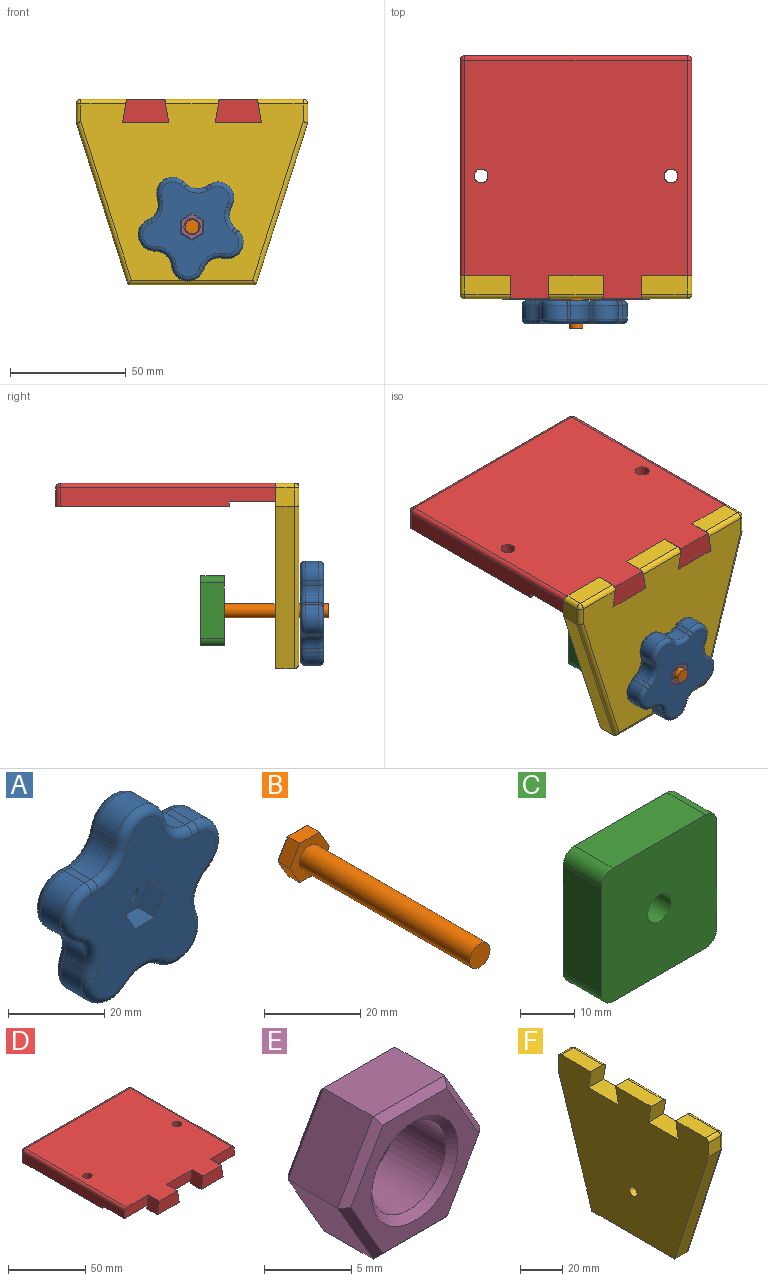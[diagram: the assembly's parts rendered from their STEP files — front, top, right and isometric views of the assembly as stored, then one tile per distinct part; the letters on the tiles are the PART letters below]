
ASSEMBLY  parts=6 mates=9
PART A: 70 faces, bbox 46.8x10x45.2 mm
  f0: plane 41.61x40.06mm, normal (0,-1,0), area 933.1mm2, adj f22,f23,f24,f25,f26,f27,f30,f31
  f1: plane 6x1.9mm, normal (0,0,1), area 11.4mm2, adj f12,f14,f34,f54
  f2: plane 6x1.81mm, normal (0.95,0,0.31), area 11.4mm2, adj f12,f15,f30,f50
  f3: plane 6x1.81mm, normal (-0.95,0,0.31), area 11.4mm2, adj f15,f16,f33,f53
  f4: plane 6x1.9mm, normal (0,0,1), area 11.4mm2, adj f16,f17,f37,f57
  f5: plane 6x1.54mm, normal (-0.59,0,-0.81), area 11.4mm2, adj f17,f18,f41,f61
  f6: plane 6x1.81mm, normal (-0.95,0,0.31), area 11.4mm2, adj f18,f20,f45,f65
  f7: plane 6x1.54mm, normal (0.59,0,-0.81), area 11.4mm2, adj f19,f20,f49,f69
  f8: plane 6x1.54mm, normal (-0.59,0,-0.81), area 11.4mm2, adj f19,f21,f46,f66
  f9: plane 6x1.81mm, normal (0.95,0,0.31), area 11.4mm2, adj f13,f21,f42,f62
  f10: plane 6x1.54mm, normal (0.59,0,-0.81), area 11.4mm2, adj f13,f14,f38,f58
  f11: plane 41.61x40.06mm, normal (0,1,0), area 991.5mm2, adj f29,f50,f51,f52,f53,f54,f55,f56
  f12: cylinder r=7mm len=6.66mm, axis (0,-1,0), area 52.8mm2, adj f1,f2,f32,f52
  f13: cylinder r=7mm len=7.83mm, axis (0,1,0), area 52.8mm2, adj f9,f10,f40,f60
  f14: cylinder r=7mm len=12.66mm, axis (0,-1,0), area 105.6mm2, adj f1,f10,f36,f56
  f15: cylinder r=7mm len=13.31mm, axis (0,-1,0), area 105.6mm2, adj f2,f3,f31,f51
  f16: cylinder r=7mm len=6.66mm, axis (0,1,0), area 52.8mm2, adj f3,f4,f35,f55
  f17: cylinder r=7mm len=12.66mm, axis (0,1,0), area 105.6mm2, adj f4,f5,f39,f59
  f18: cylinder r=7mm len=7.83mm, axis (0,1,0), area 52.8mm2, adj f5,f6,f43,f63
  f19: cylinder r=7mm len=8.23mm, axis (0,1,0), area 52.8mm2, adj f7,f8,f48,f68
  f20: cylinder r=7mm len=11.11mm, axis (0,1,0), area 105.6mm2, adj f6,f7,f47,f67
  f21: cylinder r=7mm len=11.11mm, axis (0,1,0), area 105.6mm2, adj f8,f9,f44,f64
  f22: plane 5x5mm, normal (0.87,0,-0.5), area 28.9mm2, adj f0,f23,f27,f28
  f23: plane 5x5mm, normal (0.87,0,0.5), area 28.9mm2, adj f0,f22,f24,f28
  f24: plane 5.77x5mm, normal (0,0,1), area 28.9mm2, adj f0,f23,f25,f28
  f25: plane 5x5mm, normal (-0.87,0,0.5), area 28.9mm2, adj f0,f24,f26,f28
  f26: plane 5x5mm, normal (-0.87,0,-0.5), area 28.9mm2, adj f0,f25,f27,f28
  f27: plane 5.77x5mm, normal (0,0,-1), area 28.9mm2, adj f0,f22,f26,f28
  f28: plane 11.55x10mm, normal (0,-1,0), area 58.3mm2, adj f22,f23,f24,f25,f26,f27,f29
  f29: cylinder r=3mm len=6mm, axis (0,-1,0), area 94.2mm2, adj f11,f28
  f30: cylinder r=2mm len=2.49mm, axis (0.31,0,-0.95), area 6mm2, adj f0,f2,f31,f32
  f31: torus R=5mm, axis (0,-1,0), area 49.5mm2, adj f0,f15,f30,f33
  f32: torus R=9mm, axis (0,-1,0), area 30.5mm2, adj f0,f12,f30,f34
  f33: cylinder r=2mm len=2.49mm, axis (0.31,0,0.95), area 6mm2, adj f0,f3,f31,f35
  f34: cylinder r=2mm len=2mm, axis (1,0,0), area 6mm2, adj f0,f1,f32,f36
  f35: torus R=9mm, axis (0,-1,0), area 30.5mm2, adj f0,f16,f33,f37
  f36: torus R=5mm, axis (0,-1,0), area 49.5mm2, adj f0,f14,f34,f38
  f37: cylinder r=2mm len=2mm, axis (1,0,0), area 6mm2, adj f0,f4,f35,f39
  f38: cylinder r=2mm len=2.74mm, axis (-0.81,0,-0.59), area 6mm2, adj f0,f10,f36,f40
  f39: torus R=5mm, axis (0,-1,0), area 49.5mm2, adj f0,f17,f37,f41
  f40: torus R=9mm, axis (0,-1,0), area 30.5mm2, adj f0,f13,f38,f42
  f41: cylinder r=2mm len=2.74mm, axis (-0.81,0,0.59), area 6mm2, adj f0,f5,f39,f43
  f42: cylinder r=2mm len=2.49mm, axis (0.31,0,-0.95), area 6mm2, adj f0,f9,f40,f44
  f43: torus R=9mm, axis (0,-1,0), area 30.5mm2, adj f0,f18,f41,f45
  f44: torus R=5mm, axis (0,-1,0), area 49.5mm2, adj f0,f21,f42,f46
  f45: cylinder r=2mm len=2.49mm, axis (0.31,0,0.95), area 6mm2, adj f0,f6,f43,f47
  f46: cylinder r=2mm len=2.74mm, axis (-0.81,0,0.59), area 6mm2, adj f0,f8,f44,f48
  f47: torus R=5mm, axis (0,-1,0), area 49.5mm2, adj f0,f20,f45,f49
  f48: torus R=9mm, axis (0,-1,0), area 30.5mm2, adj f0,f19,f46,f49
  f49: cylinder r=2mm len=2.74mm, axis (-0.81,0,-0.59), area 6mm2, adj f0,f7,f47,f48
  f50: cylinder r=2mm len=2.49mm, axis (-0.31,0,0.95), area 6mm2, adj f2,f11,f51,f52
  f51: torus R=5mm, axis (0,-1,0), area 49.5mm2, adj f11,f15,f50,f53
  f52: torus R=9mm, axis (0,-1,0), area 30.5mm2, adj f11,f12,f50,f54
  f53: cylinder r=2mm len=2.49mm, axis (-0.31,0,-0.95), area 6mm2, adj f3,f11,f51,f55
  f54: cylinder r=2mm len=2mm, axis (-1,0,0), area 6mm2, adj f1,f11,f52,f56
  f55: torus R=9mm, axis (0,-1,0), area 30.5mm2, adj f11,f16,f53,f57
  f56: torus R=5mm, axis (0,-1,0), area 49.5mm2, adj f11,f14,f54,f58
  f57: cylinder r=2mm len=2mm, axis (-1,0,0), area 6mm2, adj f4,f11,f55,f59
  f58: cylinder r=2mm len=2.74mm, axis (0.81,0,0.59), area 6mm2, adj f10,f11,f56,f60
  f59: torus R=5mm, axis (0,-1,0), area 49.5mm2, adj f11,f17,f57,f61
  f60: torus R=9mm, axis (0,-1,0), area 30.5mm2, adj f11,f13,f58,f62
  f61: cylinder r=2mm len=2.74mm, axis (0.81,0,-0.59), area 6mm2, adj f5,f11,f59,f63
  f62: cylinder r=2mm len=2.49mm, axis (-0.31,0,0.95), area 6mm2, adj f9,f11,f60,f64
  f63: torus R=9mm, axis (0,-1,0), area 30.5mm2, adj f11,f18,f61,f65
  f64: torus R=5mm, axis (0,-1,0), area 49.5mm2, adj f11,f21,f62,f66
  f65: cylinder r=2mm len=2.49mm, axis (-0.31,0,-0.95), area 6mm2, adj f6,f11,f63,f67
  f66: cylinder r=2mm len=2.74mm, axis (0.81,0,-0.59), area 6mm2, adj f8,f11,f64,f68
  f67: torus R=5mm, axis (0,-1,0), area 49.5mm2, adj f11,f20,f65,f69
  f68: torus R=9mm, axis (0,-1,0), area 30.5mm2, adj f11,f19,f66,f69
  f69: cylinder r=2mm len=2.74mm, axis (0.81,0,0.59), area 6mm2, adj f7,f11,f67,f68
PART B: 16 faces, bbox 11.5x54x10 mm
  f0: plane 5x3.5mm, normal (-0.87,0,0.5), area 20.2mm2, adj f1,f5,f7,f15
  f1: plane 5x3.5mm, normal (-0.87,0,-0.5), area 20.2mm2, adj f0,f2,f7,f13
  f2: plane 5.77x3.5mm, normal (0,0,-1), area 20.2mm2, adj f1,f3,f7,f11
  f3: plane 5x3.5mm, normal (0.87,0,-0.5), area 20.2mm2, adj f2,f4,f7,f10
  f4: plane 5x3.5mm, normal (0.87,0,0.5), area 20.2mm2, adj f3,f5,f7,f12
  f5: plane 5.77x3.5mm, normal (0,0,1), area 20.2mm2, adj f0,f4,f7,f14
  f6: plane 10.39x9mm, normal (0,1,0), area 70.1mm2, adj f10,f11,f12,f13,f14,f15
  f7: plane 11.55x10mm, normal (0,-1,0), area 58.3mm2, adj f0,f1,f2,f3,f4,f5,f8
  f8: cylinder r=3mm len=50mm, axis (0,1,0), area 942.5mm2, adj f7,f9
  f9: plane 6x6mm, normal (0,-1,0), area 28.3mm2, adj f8
  f10: plane 5x3.18mm, normal (0.61,0.71,-0.35), area 3.9mm2, adj f3,f6,f11,f12
  f11: plane 5.77x0.5mm, normal (0,0.71,-0.71), area 3.9mm2, adj f2,f6,f10,f13
  f12: plane 5x3.18mm, normal (0.61,0.71,0.35), area 3.9mm2, adj f4,f6,f10,f14
  f13: plane 5x3.18mm, normal (-0.61,0.71,-0.35), area 3.9mm2, adj f1,f6,f11,f15
  f14: plane 5.77x0.5mm, normal (0,0.71,0.71), area 3.9mm2, adj f5,f6,f12,f15
  f15: plane 5x3.18mm, normal (-0.61,0.71,0.35), area 3.9mm2, adj f0,f6,f13,f14
PART C: 18 faces, bbox 30x10x30 mm
  f0: plane 30x30mm, normal (0,1,0), area 805.7mm2, adj f1,f2,f3,f4,f6,f7,f8,f9
  f1: plane 24x10mm, normal (0,0,-1), area 240mm2, adj f0,f5,f14,f17
  f2: plane 24x10mm, normal (1,0,0), area 240mm2, adj f0,f5,f14,f15
  f3: plane 24x10mm, normal (0,0,1), area 240mm2, adj f0,f5,f15,f16
  f4: plane 24x10mm, normal (-1,0,0), area 240mm2, adj f0,f5,f16,f17
  f5: plane 30x30mm, normal (0,-1,0), area 864mm2, adj f1,f2,f3,f4,f13,f14,f15,f16
  f6: plane 5x5mm, normal (-0.87,0,-0.5), area 28.9mm2, adj f0,f7,f11,f12
  f7: plane 5x5mm, normal (-0.87,0,0.5), area 28.9mm2, adj f0,f6,f8,f12
  f8: plane 5.77x5mm, normal (0,0,1), area 28.9mm2, adj f0,f7,f9,f12
  f9: plane 5x5mm, normal (0.87,0,0.5), area 28.9mm2, adj f0,f8,f10,f12
  f10: plane 5x5mm, normal (0.87,0,-0.5), area 28.9mm2, adj f0,f9,f11,f12
  f11: plane 5.77x5mm, normal (0,0,-1), area 28.9mm2, adj f0,f6,f10,f12
  f12: plane 11.55x10mm, normal (0,1,0), area 58.3mm2, adj f6,f7,f8,f9,f10,f11,f13
  f13: cylinder r=3mm len=6mm, axis (0,1,0), area 94.2mm2, adj f5,f12
  f14: cylinder r=3mm len=10mm, axis (0,1,0), area 47.1mm2, adj f0,f1,f2,f5
  f15: cylinder r=3mm len=10mm, axis (0,-1,0), area 47.1mm2, adj f0,f2,f3,f5
  f16: cylinder r=3mm len=10mm, axis (0,1,0), area 47.1mm2, adj f0,f3,f4,f5
  f17: cylinder r=3mm len=10mm, axis (0,-1,0), area 47.1mm2, adj f0,f1,f4,f5
PART D: 29 faces, bbox 100x105x10 mm
  f0: plane 100x75mm, normal (0,0,-1), area 7441.7mm2, adj f9,f10,f11,f12,f13,f18,f24,f27
  f1: plane 20x10mm, normal (0,0,-1), area 200mm2, adj f5,f15,f17,f25
  f2: plane 23.53x8mm, normal (0,-1,0), area 176.9mm2, adj f7,f14,f15,f28
  f3: plane 21.76x8mm, normal (0,-1,0), area 167.6mm2, adj f7,f11,f16,f19,f28
  f4: plane 21.76x8mm, normal (0,-1,0), area 167.6mm2, adj f7,f10,f17,f22,f28
  f5: plane 20x10mm, normal (0,-1,0), area 182.4mm2, adj f1,f7,f15,f17
  f6: plane 20x10mm, normal (0,-1,0), area 182.4mm2, adj f7,f8,f14,f16
  f7: plane 103x96mm, normal (0,0,1), area 9200.9mm2, adj f2,f3,f4,f5,f6,f12,f13,f14
  f8: plane 20x10mm, normal (0,0,-1), area 200mm2, adj f6,f14,f16,f26
  f9: plane 96x8mm, normal (0,1,0), area 768mm2, adj f0,f18,f21,f24
  f10: plane 93x8mm, normal (-1,0,0), area 704mm2, adj f0,f4,f22,f24,f27,f28
  f11: plane 93x8mm, normal (1,0,0), area 704mm2, adj f0,f3,f18,f19,f27,f28
  f12: cylinder r=3mm len=10mm, axis (0,0,1), area 188.5mm2, adj f0,f7
  f13: cylinder r=3mm len=10mm, axis (0,0,1), area 188.5mm2, adj f0,f7
  f14: plane 10x10mm, normal (-0.98,0,0.17), area 101.5mm2, adj f2,f6,f7,f8,f26
  f15: plane 10x10mm, normal (0.98,0,0.17), area 101.5mm2, adj f1,f2,f5,f7,f25
  f16: plane 10x10mm, normal (0.98,0,0.17), area 101.5mm2, adj f3,f6,f7,f8,f26
  f17: plane 10x10mm, normal (-0.98,0,0.17), area 101.5mm2, adj f1,f4,f5,f7,f25
  f18: cylinder r=2mm len=8mm, axis (0,0,1), area 25.1mm2, adj f0,f9,f11,f20
  f19: cylinder r=2mm len=93mm, axis (0,-1,0), area 292.2mm2, adj f3,f7,f11,f20
  f20: sphere r=2mm, area 6.3mm2, adj f18,f19,f21
  f21: cylinder r=2mm len=96mm, axis (1,0,0), area 301.6mm2, adj f7,f9,f20,f23
  f22: cylinder r=2mm len=93mm, axis (0,1,0), area 292.2mm2, adj f4,f7,f10,f23
  f23: sphere r=2mm, area 6.3mm2, adj f21,f22,f24
  f24: cylinder r=2mm len=8mm, axis (0,0,-1), area 25.1mm2, adj f0,f9,f10,f23
  f25: plane 20x2mm, normal (0,1,0), area 39.3mm2, adj f1,f15,f17,f28
  f26: plane 20x2mm, normal (0,1,0), area 39.3mm2, adj f8,f14,f16,f28
  f27: plane 100x2mm, normal (0,-1,0), area 200mm2, adj f0,f10,f11,f28
  f28: plane 100x20mm, normal (0,0,-1), area 2000mm2, adj f2,f3,f4,f10,f11,f25,f26,f27
PART E: 23 faces, bbox 11.5x5x10 mm
  f0: plane 5x4mm, normal (-0.87,0,0.5), area 23.1mm2, adj f1,f6,f15,f22
  f1: plane 5x4mm, normal (-0.87,0,-0.5), area 23.1mm2, adj f0,f2,f13,f20
  f2: plane 5.77x4mm, normal (0,0,-1), area 23.1mm2, adj f1,f3,f11,f18
  f3: plane 5x4mm, normal (0.87,0,-0.5), area 23.1mm2, adj f2,f4,f10,f17
  f4: plane 5x4mm, normal (0.87,0,0.5), area 23.1mm2, adj f3,f6,f12,f19
  f5: cylinder r=3mm len=6mm, axis (0,1,0), area 75.4mm2, adj f9,f16
  f6: plane 5.77x4mm, normal (0,0,1), area 23.1mm2, adj f0,f4,f14,f21
  f7: plane 10.39x9mm, normal (0,-1,0), area 31.7mm2, adj f16,f17,f18,f19,f20,f21,f22
  f8: plane 10.39x9mm, normal (0,1,0), area 31.7mm2, adj f9,f10,f11,f12,f13,f14,f15
  f9: cone r=3.5mm half-angle=45deg, axis (0,1,0), area 14.4mm2, adj f5,f8
  f10: plane 5x3.18mm, normal (0.61,0.71,-0.35), area 3.9mm2, adj f3,f8,f11,f12
  f11: plane 5.77x0.5mm, normal (0,0.71,-0.71), area 3.9mm2, adj f2,f8,f10,f13
  f12: plane 5x3.18mm, normal (0.61,0.71,0.35), area 3.9mm2, adj f4,f8,f10,f14
  f13: plane 5x3.18mm, normal (-0.61,0.71,-0.35), area 3.9mm2, adj f1,f8,f11,f15
  f14: plane 5.77x0.5mm, normal (0,0.71,0.71), area 3.9mm2, adj f6,f8,f12,f15
  f15: plane 5x3.18mm, normal (-0.61,0.71,0.35), area 3.9mm2, adj f0,f8,f13,f14
  f16: cone r=3mm half-angle=45deg, axis (0,-1,0), area 14.4mm2, adj f5,f7
  f17: plane 5x3.18mm, normal (0.61,-0.71,-0.35), area 3.9mm2, adj f3,f7,f18,f19
  f18: plane 5.77x0.5mm, normal (0,-0.71,-0.71), area 3.9mm2, adj f2,f7,f17,f20
  f19: plane 5x3.18mm, normal (0.61,-0.71,0.35), area 3.9mm2, adj f4,f7,f17,f21
  f20: plane 5x3.18mm, normal (-0.61,-0.71,-0.35), area 3.9mm2, adj f1,f7,f18,f22
  f21: plane 5.77x0.5mm, normal (0,-0.71,0.71), area 3.9mm2, adj f6,f7,f19,f22
  f22: plane 5x3.18mm, normal (-0.61,-0.71,0.35), area 3.9mm2, adj f0,f7,f20,f21
PART F: 29 faces, bbox 10x100x80 mm
  f0: plane 8x8mm, normal (0,1,0), area 64mm2, adj f13,f15,f24,f27
  f1: plane 19.76x8mm, normal (0,0,1), area 158.1mm2, adj f2,f15,f25,f27
  f2: plane 10x10mm, normal (0,-0.98,-0.17), area 100.7mm2, adj f1,f3,f14,f15,f25
  f3: plane 20x10mm, normal (0,0,1), area 200mm2, adj f2,f4,f14,f15
  f4: plane 10x10mm, normal (0,0.98,-0.17), area 100.7mm2, adj f3,f5,f14,f15,f28
  f5: plane 23.53x8mm, normal (0,0,1), area 188.2mm2, adj f4,f6,f15,f28
  f6: plane 10x10mm, normal (0,-0.98,-0.17), area 100.7mm2, adj f5,f7,f14,f15,f28
  f7: plane 20x10mm, normal (0,0,1), area 200mm2, adj f6,f8,f14,f15
  f8: plane 10x10mm, normal (0,0.98,-0.17), area 100.7mm2, adj f7,f9,f14,f15,f18
  f9: plane 19.76x8mm, normal (0,0,1), area 158.1mm2, adj f8,f15,f17,f18
  f10: plane 8x8mm, normal (0,-1,0), area 64mm2, adj f11,f15,f17,f20
  f11: plane 70x22.4mm, normal (0,-0.95,-0.3), area 588mm2, adj f10,f12,f15,f21
  f12: plane 55.21x8mm, normal (0,0,-1), area 441.7mm2, adj f11,f13,f15,f22
  f13: plane 70x22.4mm, normal (0,0.95,-0.3), area 588mm2, adj f0,f12,f15,f23
  f14: plane 96x76mm, normal (1,0,0), area 5484.7mm2, adj f2,f3,f4,f6,f7,f8,f16,f18
  f15: plane 100x80mm, normal (-1,0,0), area 6045mm2, adj f0,f1,f2,f3,f4,f5,f6,f7
  f16: cylinder r=2.58mm len=10mm, axis (1,0,0), area 161.8mm2, adj f14,f15
  f17: cylinder r=2mm len=8mm, axis (-1,0,0), area 25.1mm2, adj f9,f10,f15,f19
  f18: cylinder r=2mm len=19.76mm, axis (0,1,0), area 61.7mm2, adj f8,f9,f14,f19
  f19: sphere r=2mm, area 6.3mm2, adj f17,f18,f20
  f20: cylinder r=2mm len=8mm, axis (0,0,1), area 24.8mm2, adj f10,f14,f19,f21
  f21: cylinder r=2mm len=70.61mm, axis (0,-0.3,0.95), area 228.9mm2, adj f11,f14,f20,f22
  f22: cylinder r=2mm len=55.21mm, axis (0,-1,0), area 170.1mm2, adj f12,f14,f21,f23
  f23: cylinder r=2mm len=70.61mm, axis (0,-0.3,-0.95), area 228.9mm2, adj f13,f14,f22,f24
  f24: cylinder r=2mm len=8mm, axis (0,0,-1), area 24.8mm2, adj f0,f14,f23,f26
  f25: cylinder r=2mm len=19.76mm, axis (0,1,0), area 61.7mm2, adj f1,f2,f14,f26
  f26: sphere r=2mm, area 6.3mm2, adj f24,f25,f27
  f27: cylinder r=2mm len=8mm, axis (-1,0,0), area 25.1mm2, adj f0,f1,f15,f26
  f28: cylinder r=2mm len=23.53mm, axis (0,1,0), area 73.1mm2, adj f4,f5,f6,f14
PLACE A rot(axis=(0,-1,0),30deg) t=(-50.27,-62.99,-31.49)mm
PLACE B t=(-50.27,-25.05,-31.49)mm
PLACE C t=(-50.27,-20.05,-31.49)mm
PLACE D t=(-50.27,-62.31,13.51)mm
PLACE E rot(axis=(0,-1,0),90deg) t=(-50.27,-67.99,-31.49)mm
PLACE F rot(axis=(0,0,-1),90deg) t=(-50.27,-52.31,13.51)mm
MATE planar E.f3 <-> A.f26  axis (0.5,0,0.87) through (-47.77,-70.49,-27.16)mm
MATE planar D.f8 <-> F.f3  axis (0,0,-1) through (-30.27,-57.31,13.51)mm
MATE planar D.f3 <-> F.f15  axis (0,-1,0) through (-10.85,-52.31,19.54)mm
MATE cylindrical B.f8 <-> F.f16  axis (0,1,0) through (-50.27,-50.05,-31.49)mm
MATE planar C.f13 <-> B.f7  axis (0,1,0) through (-50.27,-25.05,-31.49)mm
MATE planar D.f16 <-> F.f2  axis (0.98,0,0.17) through (-21.15,-57.31,18.51)mm
MATE cylindrical E.f5 <-> B.f8  axis (0,1,0) through (-50.27,-72.49,-31.49)mm
MATE planar C.f10 <-> B.f0  axis (0.87,0,-0.5) through (-54.6,-22.55,-28.99)mm
MATE planar E.f5 <-> A.f28  axis (0,1,0) through (-50.27,-67.99,-31.49)mm
